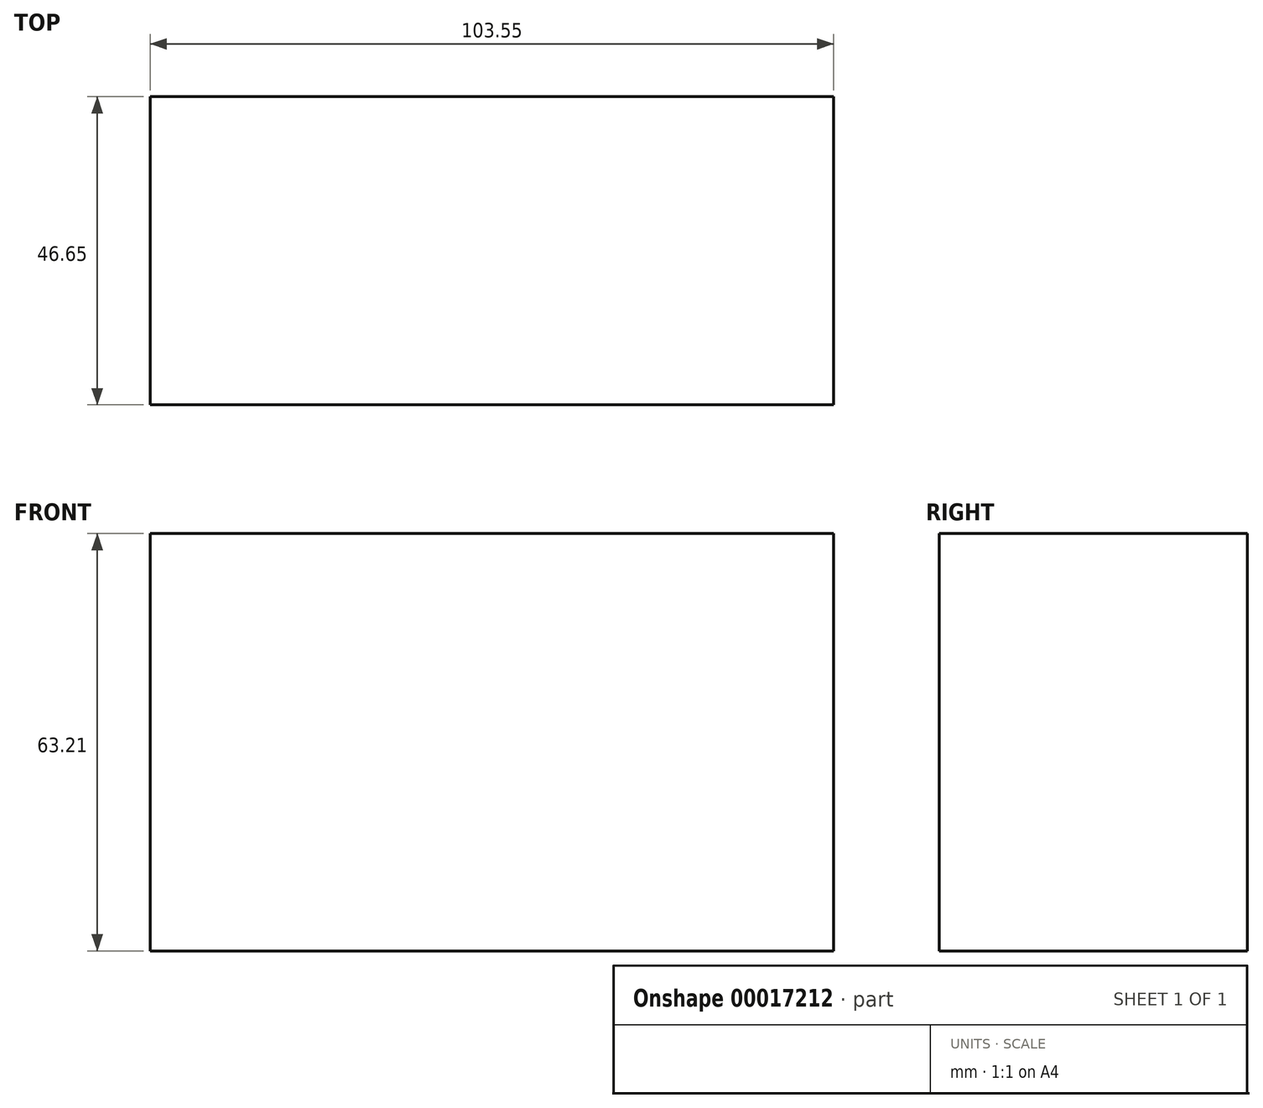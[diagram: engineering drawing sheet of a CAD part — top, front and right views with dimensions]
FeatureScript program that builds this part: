
annotation { "Feature Type Name" : "Feature", "Feature Type Description" : "" }
export const myFeature = defineFeature(function(context is Context, id is Id, definition is map)
    precondition{}
    {
        {
            var Q0;
            Q0=qCreatedBy(makeId("Front.planeOp"),FACE);
            var sketch = newSketch(context, id + "F0", { "sketchPlane" : qUnion([Q0])});
            skLineSegment(sketch, "E0.bottom", {"start": v(-103.55, 63.21) * mm, "end": v(0, 63.21) * mm});
            skLineSegment(sketch, "E0.top", {"start": v(-103.55, 0) * mm, "end": v(0, 0) * mm});
            skLineSegment(sketch, "E0.left", {"start": v(-103.55, 63.21) * mm, "end": v(-103.55, 0) * mm});
            skLineSegment(sketch, "E0.right", {"start": v(0, 63.21) * mm, "end": v(0, 0) * mm});
            skSolve(sketch);
        }
        {
            var Q0;
            Q0 = qSketchRegion(id + "F0", true);
            extrude(context, id + "F1", {"entities" : qUnion([Q0]), "depth" : 46.65 * mm});
        }
    });
